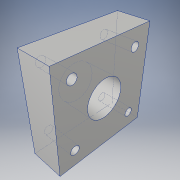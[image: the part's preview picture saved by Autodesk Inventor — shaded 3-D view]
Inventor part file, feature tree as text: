
AUTODESK INVENTOR PART (.ipt)
format: ipt  version: 2019 (Build 230136000, 136)  size: 112,128 bytes
history: native  units: in
note: dims shown in document units (in); Inventor stores cm internally (conversion verified against a paired STEP export)
features: extrude x1, sketch x1
ambient origin geometry x8: Origin, YZ Plane, XZ Plane, XY Plane, X Axis, Y Axis, Z Axis, Center Point
bodies: Solid1 (feature_tree)
feature tree (2):
  extrude  "Extrusion1"  Depth=0.5in
  sketch  "Sketch1"  dims[d0=1.5in d1=0.5781in d2=0.14in d3=1.0in d4=0.5in d5=0.0in]
